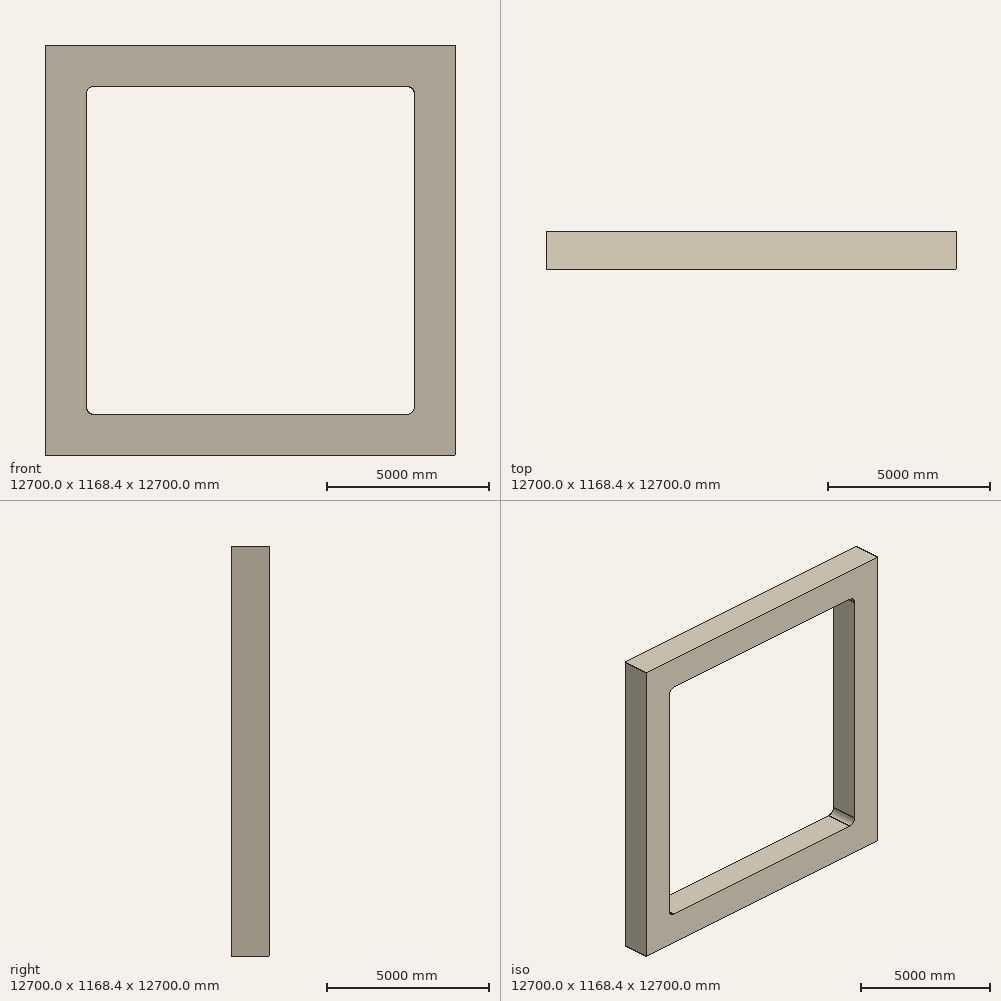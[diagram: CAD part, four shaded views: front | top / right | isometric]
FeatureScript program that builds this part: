
annotation { "Feature Type Name" : "Feature", "Feature Type Description" : "" }
export const myFeature = defineFeature(function(context is Context, id is Id, definition is map)
    precondition{}
    {
        {
            var Q0;
            Q0=qCreatedBy(makeId("Front.planeOp"),FACE);
            var sketch = newSketch(context, id + "F0", { "sketchPlane" : qUnion([Q0])});
            skLineSegment(sketch, "E0.bottom", {"start": v(6350, 6350) * mm, "end": v(-6350, 6350) * mm});
            skLineSegment(sketch, "E0.top", {"start": v(6350, -6350) * mm, "end": v(-6350, -6350) * mm});
            skLineSegment(sketch, "E0.left", {"start": v(6350, 6350) * mm, "end": v(6350, -6350) * mm});
            skLineSegment(sketch, "E0.right", {"start": v(-6350, 6350) * mm, "end": v(-6350, -6350) * mm});
            skPoint(sketch, "E0.middle", {"position": v(0, 0) * mm});
            skLineSegment(sketch, "E1.0", {"start": v(-5080, 4826) * mm, "end": v(-5080, -4826) * mm});
            skLineSegment(sketch, "E1.1", {"start": v(4826, 5080) * mm, "end": v(-4826, 5080) * mm});
            skLineSegment(sketch, "E1.2", {"start": v(5080, 4826) * mm, "end": v(5080, -4826) * mm});
            skLineSegment(sketch, "E1.3", {"start": v(4826, -5080) * mm, "end": v(-4826, -5080) * mm});
            skPoint(sketch, "E2.visualSharp", {"position": v(-5080, 5080) * mm});
            skArc(sketch, "E2.filletArc", {"start": v(-4826, 5080) * mm, "mid": v(-5005.6, 5005.6) * mm, "end": v(-5080, 4826) * mm});
            skPoint(sketch, "E3.visualSharp", {"position": v(5080, 5080) * mm});
            skArc(sketch, "E3.filletArc", {"start": v(5080, 4826) * mm, "mid": v(5005.6, 5005.6) * mm, "end": v(4826, 5080) * mm});
            skPoint(sketch, "E4.visualSharp", {"position": v(-5080, -5080) * mm});
            skArc(sketch, "E4.filletArc", {"start": v(-5080, -4826) * mm, "mid": v(-5005.6, -5005.6) * mm, "end": v(-4826, -5080) * mm});
            skPoint(sketch, "E5.visualSharp", {"position": v(5080, -5080) * mm});
            skArc(sketch, "E5.filletArc", {"start": v(4826, -5080) * mm, "mid": v(5005.6, -5005.6) * mm, "end": v(5080, -4826) * mm});
            skSolve(sketch);
        }
        {
            var Q0;
            Q0=makeQuery(id+"F0.imprint","IMPRINT",FACE,{"disambiguationData":[TD([[makeQuery(id+"F0.imprint","IMPRINT",EDGE,{"derivedFrom":sQuery(id+"F0.wireOp",EDGE,"E0.bottom")}),1.0]])]});
            extrude(context, id + "F1", {"entities" : qUnion([Q0]), "depth" : 1168.4 * mm});
        }
        {
            var Q0;
            Q0=makeQuery(id+"F1.opExtrude","CAP_EDGE",EDGE,{"disambiguationData":[OSD([sQuery(id+"F0.wireOp",EDGE,"E1.3")])],"isStart":true});
            var Q1;
            Q1=makeQuery(id+"F1.opExtrude","CAP_EDGE",EDGE,{"disambiguationData":[OSD([sQuery(id+"F0.wireOp",EDGE,"E1.0")])],"isStart":true});
            var Q2;
            Q2=makeQuery(id+"F1.opExtrude","CAP_EDGE",EDGE,{"disambiguationData":[OSD([sQuery(id+"F0.wireOp",EDGE,"E1.2")])],"isStart":true});
            var Q3;
            Q3=makeQuery(id+"F1.opExtrude","CAP_EDGE",EDGE,{"disambiguationData":[OSD([sQuery(id+"F0.wireOp",EDGE,"E1.1")])],"isStart":true});
            fillet(context, id + "F2", {"entities" : qUnion([Q0, Q1, Q2, Q3]), "radius" : 5.08 * mm, "tangentPropagation" : true, "rho" : 0.5, "crossSection" : FilletCrossSection.CONIC, "allowEdgeOverflow" : false});
        }
    });
